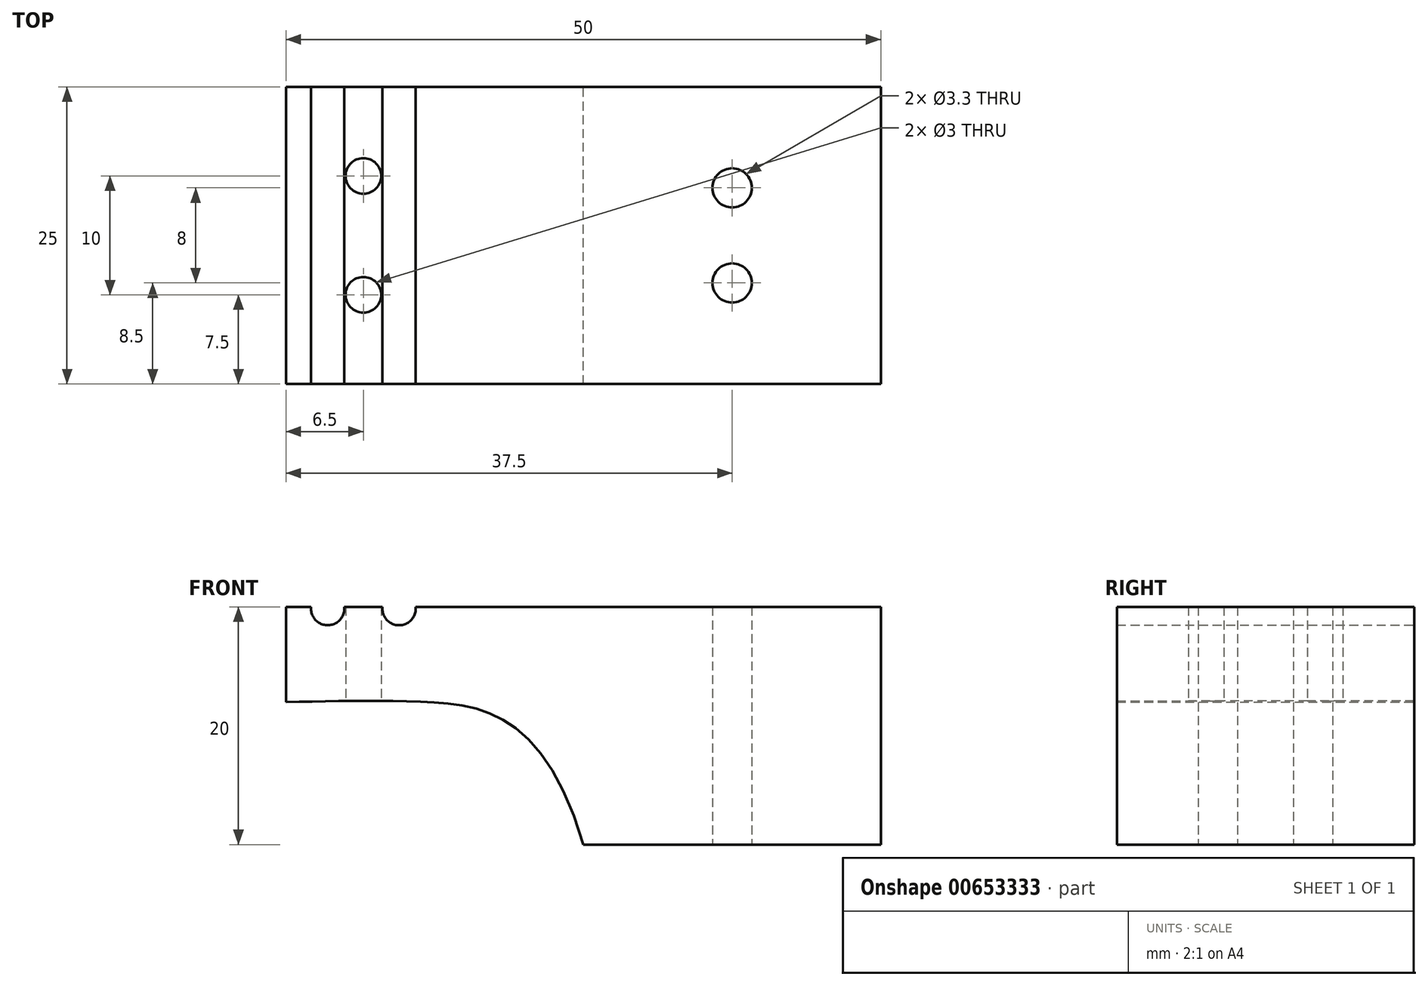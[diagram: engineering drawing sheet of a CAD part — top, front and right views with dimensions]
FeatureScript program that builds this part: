
annotation { "Feature Type Name" : "Feature", "Feature Type Description" : "" }
export const myFeature = defineFeature(function(context is Context, id is Id, definition is map)
    precondition{}
    {
        {
            var Q0;
            Q0=qCreatedBy(makeId("Top.planeOp"),FACE);
            var sketch = newSketch(context, id + "F0", { "sketchPlane" : qUnion([Q0])});
            skLineSegment(sketch, "E0.bottom", {"start": v(-12.5, 12.5) * mm, "end": v(12.5, 12.5) * mm});
            skLineSegment(sketch, "E0.top", {"start": v(-12.5, -12.5) * mm, "end": v(12.5, -12.5) * mm});
            skLineSegment(sketch, "E0.left", {"start": v(-12.5, 12.5) * mm, "end": v(-12.5, -12.5) * mm});
            skLineSegment(sketch, "E0.right", {"start": v(12.5, 12.5) * mm, "end": v(12.5, -12.5) * mm});
            skCircle(sketch, "E1", {"center": v(0, -4) * mm, "radius": 1.65 * mm});
            skCircle(sketch, "E2", {"center": v(0, 4) * mm, "radius": 1.65 * mm});
            skSolve(sketch);
        }
        {
            var Q0;
            Q0=makeQuery(id+"F0.imprint","IMPRINT",FACE,{"disambiguationData":[TD([[makeQuery(id+"F0.imprint","IMPRINT",EDGE,{"derivedFrom":sQuery(id+"F0.wireOp",EDGE,"E0.bottom")}),-1.0]])]});
            extrude(context, id + "F1", {"entities" : qUnion([Q0]), "depth" : 20 * mm, "offsetDistance" : 25 * mm});
        }
        {
            var Q0;
            Q0=makeQuery(id+"F1.opExtrude","SWEPT_FACE",FACE,{"disambiguationData":[OSD([sQuery(id+"F0.wireOp",EDGE,"E0.left")])]});
            extrude(context, id + "F2", {"entities" : qUnion([Q0]), "operationType" : NewBodyOperationType.ADD, "depth" : 25 * mm, "offsetDistance" : 25 * mm});
        }
        {
            var Q0;
            Q0=qCreatedBy(makeId("Front.planeOp"),FACE);
            var sketch = newSketch(context, id + "F3", { "sketchPlane" : qUnion([Q0])});
            skFitSpline(sketch, "E3", {"points": [v(-37.5, 12) * mm, v(-25.94, 12) * mm, v(-12.5, 0) * mm], "startDerivative": vector(25.1, 0.34) * mm, "endDerivative": vector(17.94, -60.1) * mm});
            skLineSegment(sketch, "E4", {"start": v(-37.5, 12) * mm, "end": v(-37.5, 0) * mm});
            skLineSegment(sketch, "E5", {"start": v(-37.5, 0) * mm, "end": v(-12.5, 0) * mm});
            skCircle(sketch, "E6", {"center": v(-34, 19.85) * mm, "radius": 1.4 * mm});
            skCircle(sketch, "E7", {"center": v(-28, 19.85) * mm, "radius": 1.4 * mm});
            skSolve(sketch);
        }
        {
            var Q0;
            Q0 = qSketchRegion(id + "F3", true);
            extrude(context, id + "F4", {"entities" : qUnion([Q0]), "operationType" : NewBodyOperationType.REMOVE, "endBound" : BoundingType.SYMMETRIC, "depth" : 25 * mm, "offsetDistance" : 25 * mm});
        }
        {
            var Q0;
            Q0=qCreatedBy(makeId("Top.planeOp"),FACE);
            var sketch = newSketch(context, id + "F5", { "sketchPlane" : qUnion([Q0])});
            skPoint(sketch, "E8", {"position": v(-31, 5) * mm});
            skPoint(sketch, "E9", {"position": v(-31, -5) * mm});
            skSolve(sketch);
        }
        {
            var Q0;
            Q0=sQuery(id+"F5.wireOp",VERTEX,"E9");
            var Q1;
            Q1=sQuery(id+"F5.wireOp",VERTEX,"E8");
            var Q2;
            Q2=makeQuery(id+"F1.opExtrude","SWEPT_BODY",BODY,{"disambiguationData":[OSD([sQuery(id+"F0.wireOp",EDGE,"E0.bottom"),sQuery(id+"F0.wireOp",EDGE,"E0.top"),sQuery(id+"F0.wireOp",EDGE,"E0.left"),sQuery(id+"F0.wireOp",EDGE,"E0.right"),sQuery(id+"F0.wireOp",EDGE,"E1"),sQuery(id+"F0.wireOp",EDGE,"E2")])]});
            hole(context, id + "F6", {"style" : HoleStyle.SIMPLE, "endStyle" : HoleEndStyle.THROUGH, "oppositeDirection" : true, "standardTappedOrClearance" : lookupTablePath({ "standard" : "ISO", "size" : "3", "type" : "Drilled" }), "standardBlindInLast" : lookupTablePath({ "standard" : "ISO", "size" : "3", "type" : "Drilled" }), "holeDiameter" : 3 * mm, "majorDiameter" : 5 * mm, "isTappedThrough" : true, "tappedDepth" : 6 * mm, "tapClearance" : 3, "startFromSketch" : true, "locations" : qUnion([Q0, Q1]), "scope" : qUnion([Q2])});
        }
    });
